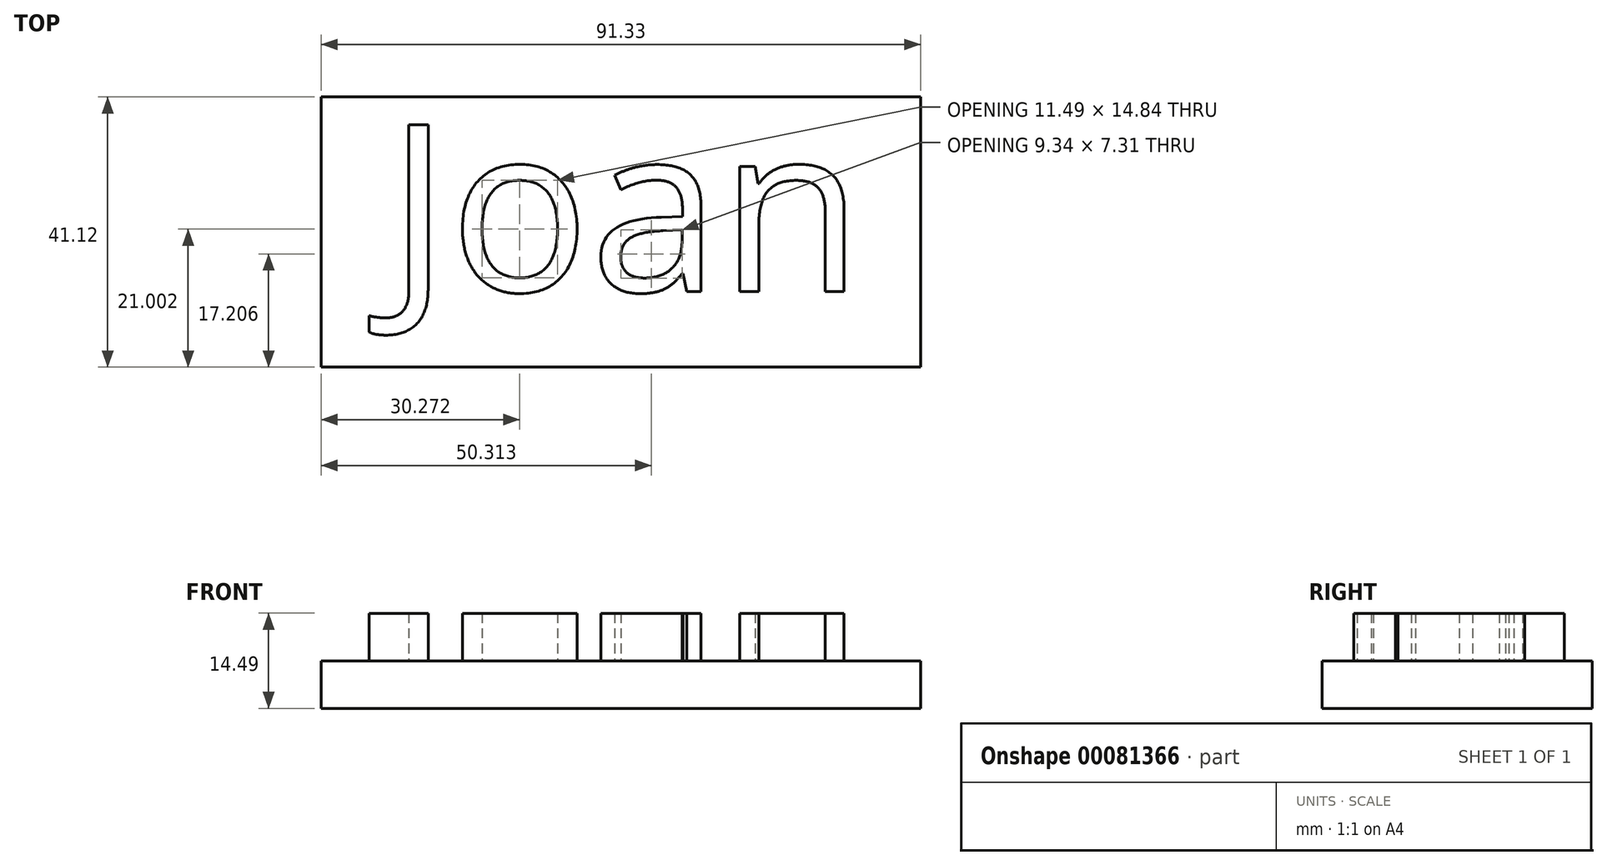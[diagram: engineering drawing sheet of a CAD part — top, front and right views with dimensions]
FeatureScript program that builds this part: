
annotation { "Feature Type Name" : "Feature", "Feature Type Description" : "" }
export const myFeature = defineFeature(function(context is Context, id is Id, definition is map)
    precondition{}
    {
        {
            var Q0;
            Q0=qCreatedBy(makeId("Top.planeOp"),FACE);
            var sketch = newSketch(context, id + "F0", { "sketchPlane" : qUnion([Q0])});
            skText(sketch, "E0", { "text": "Joan\n", "fontName": "OpenSans-Regular.ttf"});
            const initialGuessF0  = {"E0": [-0.04937, -0.00682, 1, 0, 0.02556]};
            skSetInitialGuess(sketch, initialGuessF0);
            skSolve(sketch);
        }
        {
            var Q0;
            Q0 = qSketchRegion(id + "F0", true);
            extrude(context, id + "F1", {"entities" : qUnion([Q0]), "depth" : 7.26 * mm});
        }
        {
            var Q0;
            Q0=qCreatedBy(makeId("Top.planeOp"),FACE);
            var sketch = newSketch(context, id + "F2", { "sketchPlane" : qUnion([Q0])});
            skLineSegment(sketch, "E1.bottom", {"start": v(-59.44, 22.78) * mm, "end": v(31.89, 22.78) * mm});
            skLineSegment(sketch, "E1.top", {"start": v(-59.44, -18.34) * mm, "end": v(31.89, -18.34) * mm});
            skLineSegment(sketch, "E1.left", {"start": v(-59.44, 22.78) * mm, "end": v(-59.44, -18.34) * mm});
            skLineSegment(sketch, "E1.right", {"start": v(31.89, 22.78) * mm, "end": v(31.89, -18.34) * mm});
            skSolve(sketch);
        }
        {
            var Q0;
            Q0=makeQuery(id+"F2.imprint","IMPRINT",FACE,{"disambiguationData":[TD([[makeQuery(id+"F2.imprint","IMPRINT",EDGE,{"derivedFrom":sQuery(id+"F2.wireOp",EDGE,"E1.bottom")}),-1.0]])]});
            extrude(context, id + "F3", {"entities" : qUnion([Q0]), "oppositeDirection" : true, "depth" : 7.23 * mm});
        }
    });
